# Revit family: Composite Decking-Section
name_source: partatom
category: Detail Items
revit_build: Autodesk Revit Architecture 2012 (Build: 20110210_1515)
units: mm (PartAtom-declared; Revit-internal decimal feet)

## types (28) — shared parameters

## per-type parameters (varying)
| type | Gauge | Height | Keynote | Rib Max | Rib Min | Width |
| 1.5 MR 16 | 16 | 1 1/2" | 05 31 00.A1 | 4 1/4" | 3 1/2" | 6" |
| 1.5 RR 16 | 16 | 1 1/2" | 05 31 00.A8 | 2 7/16" | 1 11/16" | 6" |
| 2.0 WR 16 | 16 | 2" | 05 31 00.A15 | 6 15/16" | 5" | 12" |
| 3.0 WR 16 | 16 | 3" | 05 31 00.A22 | 7 3/16" | 4 5/8" | 12" |
| 1.5 MR 17 | 17 | 1 1/2" | 05 31 00.A2 | 4 1/4" | 3 1/2" | 6" |
| 1.5 MR 18 | 18 | 1 1/2" | 05 31 00.A3 | 4 1/4" | 3 1/2" | 6" |
| 1.5 MR 19 | 19 | 1 1/2" | 05 31 00.A4 | 4 1/4" | 3 1/2" | 6" |
| 1.5 MR 20 | 20 | 1 1/2" | 05 31 00.A5 | 4 1/4" | 3 1/2" | 6" |
| 1.5 MR 21 | 21 | 1 1/2" | 05 31 00.A6 | 4 1/4" | 3 1/2" | 6" |
| 1.5 MR 22 | 22 | 1 1/2" | 05 31 00.A7 | 4 1/4" | 3 1/2" | 6" |
| 1.5 RR 17 | 17 | 1 1/2" | 05 31 00.A9 | 2 7/16" | 1 11/16" | 6" |
| 1.5 RR 18 | 18 | 1 1/2" | 05 31 00.A10 | 2 7/16" | 1 11/16" | 6" |
| 1.5 RR 19 | 19 | 1 1/2" | 05 31 00.A11 | 2 7/16" | 1 11/16" | 6" |
| 1.5 RR 20 | 20 | 1 1/2" | 05 31 00.A12 | 2 7/16" | 1 11/16" | 6" |
| 1.5 RR 21 | 21 | 1 1/2" | 05 31 00.A13 | 2 7/16" | 1 11/16" | 6" |
| 1.5 RR 22 | 22 | 1 1/2" | 05 31 00.A14 | 2 7/16" | 1 11/16" | 6" |
| 2.0 WR 17 | 17 | 2" | 05 31 00.A16 | 6 15/16" | 5" | 12" |
| 2.0 WR 18 | 18 | 2" | 05 31 00.A17 | 6 15/16" | 5" | 12" |
| 2.0 WR 19 | 19 | 2" | 05 31 00.A18 | 6 15/16" | 5" | 12" |
| 2.0 WR 20 | 20 | 2" | 05 31 00.A19 | 6 15/16" | 5" | 12" |
| 2.0 WR 21 | 21 | 2" | 05 31 00.A20 | 6 15/16" | 5" | 12" |
| 2.0 WR 22 | 22 | 2" | 05 31 00.A21 | 6 15/16" | 5" | 12" |
| 3.0 WR 17 | 17 | 3" | 05 31 00.A23 | 7 3/16" | 4 5/8" | 12" |
| 3.0 WR 18 | 18 | 3" | 05 31 00.A24 | 7 3/16" | 4 5/8" | 12" |
| 3.0 WR 19 | 19 | 3" | 05 31 00.A25 | 7 3/16" | 4 5/8" | 12" |
| 3.0 WR 20 | 20 | 3" | 05 31 00.A26 | 7 3/16" | 4 5/8" | 12" |
| 3.0 WR 21 | 21 | 3" | 05 31 00.A27 | 7 3/16" | 4 5/8" | 12" |
| 3.0 WR 22 | 22 | 3" | 05 31 00.A28 | 7 3/16" | 4 5/8" | 12" |
